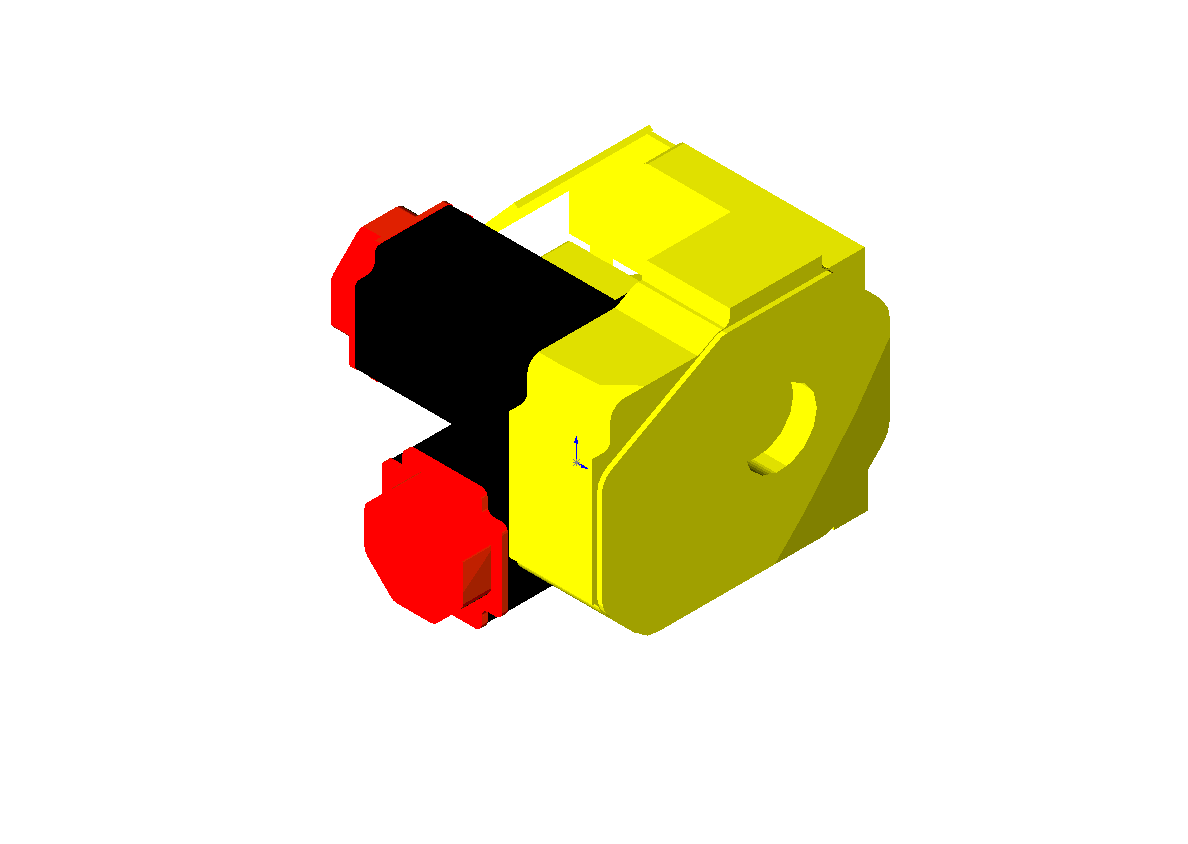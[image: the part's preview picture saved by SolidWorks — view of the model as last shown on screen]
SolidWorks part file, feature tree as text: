
SOLIDWORKS PART (.sldprt)
format: sldprt  version: not decoded by parser v0  size: 530,944 bytes
history: native  units: mm
features: sketch x16, extrude x15, plane x3, material x1, cut_extrude x1 (+9 scaffold rows collapsed)
feature tree (45):
  scaffold x9  (default folders/planes/origin — collapsed)
  material  "Material <not specified>"
  plane  "FRONT"
  plane  "TOP"
  plane  "SIDE"
  sketch  "Sketch7"
  extrude  "Base-Extrude"  Depth=97.4725mm
  sketch  "Sketch9"  dims[D1=0.762mm]
  extrude  "Boss-Extrude1"  Depth=4.445mm
  sketch  "Sketch10"
  extrude  "Boss-Extrude7"  Depth=21.59mm
  sketch  "Sketch11"
  extrude  "Boss-Extrude2"  Depth=6.985mm
  sketch  "Sketch12"
  extrude  "Boss-Extrude3"  Depth=4.1275mm
  sketch  "Sketch13"  dims[D1=9.525mm]
  extrude  "Boss-Extrude4"  Depth=27.6225mm
  sketch  "Sketch15"
  extrude  "Boss-Extrude5"  Depth=63.1825mm
  sketch  "Sketch16"  dims[D1=0.762mm]
  extrude  "Boss-Extrude6"  Depth=3.4925mm
  sketch  "Sketch17"
  cut_extrude  "Cut-Extrude1"  Depth=17.78mm
  sketch  "Sketch18"
  extrude  "Boss-Extrude8"  Depth=7.9375mm
  sketch  "Sketch19"
  extrude  "Boss-Extrude9"  Depth=126.365mm
  sketch  "Sketch20"  dims[D1=0.508mm]
  extrude  "Boss-Extrude10"  Depth=3.81mm
  sketch  "Sketch21"
  extrude  "Boss-Extrude11"  Depth=21.9075mm
  sketch  "Sketch22"  dims[D1=146.05mm]
  extrude  "Boss-Extrude12"  Depth=20.1676mm
  sketch  "Sketch23"
  extrude  "Boss-Extrude13"  Depth=3.3401mm
  sketch  "Sketch24"
  extrude  "Boss-Extrude14"  Depth=3.81mm
decode coverage: 21 of 32 modeling features carry decoded parameters
note: suppression state not decoded; provenance and decode notes live in map.json
